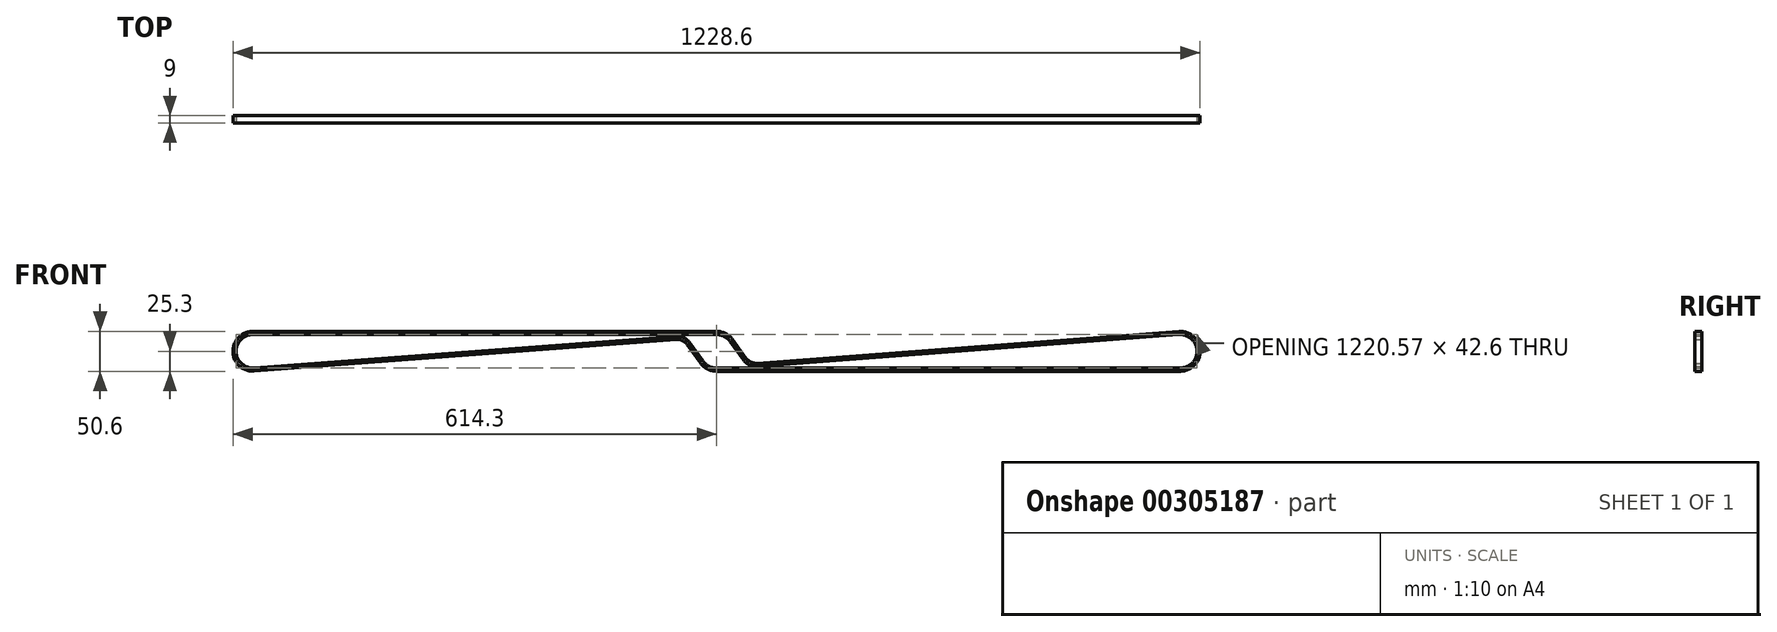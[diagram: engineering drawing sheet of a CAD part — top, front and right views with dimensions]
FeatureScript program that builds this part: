
annotation { "Feature Type Name" : "Feature", "Feature Type Description" : "" }
export const myFeature = defineFeature(function(context is Context, id is Id, definition is map)
    precondition{}
    {
        {
            var Q0;
            Q0=qCreatedBy(makeId("Front.planeOp"),FACE);
            var sketch = newSketch(context, id + "F0", { "sketchPlane" : qUnion([Q0])});
            skLineSegment(sketch, "E0", {"start": v(-36.07, 10.09) * mm, "end": v(-36.07, 10.09) * mm});
            skLineSegment(sketch, "E1", {"start": v(0, -23.3) * mm, "end": v(589, -23.3) * mm});
            skLineSegment(sketch, "E2", {"start": v(587.25, 23.23) * mm, "end": v(51.3, -17.15) * mm});
            skLineSegment(sketch, "E3", {"start": v(36.07, -10.09) * mm, "end": v(18.87, 13.66) * mm});
            skLineSegment(sketch, "E4", {"start": v(0, 23.3) * mm, "end": v(-589, 23.3) * mm});
            skLineSegment(sketch, "E5", {"start": v(-587.25, -23.23) * mm, "end": v(-51.3, 17.15) * mm});
            skArc(sketch, "E6", {"start": v(0, 23.3) * mm, "mid": v(-20.75, 10.6) * mm, "end": v(-18.87, -13.66) * mm});
            skArc(sketch, "E7", {"start": v(18.87, 13.66) * mm, "mid": v(10.6, 20.75) * mm, "end": v(0, 23.3) * mm});
            skArc(sketch, "E8", {"start": v(-18.87, -13.66) * mm, "mid": v(-10.6, -20.75) * mm, "end": v(0, -23.3) * mm});
            skArc(sketch, "E9", {"start": v(0, -23.3) * mm, "mid": v(20.75, -10.6) * mm, "end": v(18.87, 13.66) * mm});
            skLineSegment(sketch, "E10", {"start": v(-36.07, 10.09) * mm, "end": v(-18.87, -13.66) * mm});
            skArc(sketch, "E11", {"start": v(-51.3, 17.15) * mm, "mid": v(-57.24, -15.6) * mm, "end": v(-36.07, 10.09) * mm});
            skArc(sketch, "E12", {"start": v(-36.07, 10.09) * mm, "mid": v(-42.76, 15.6) * mm, "end": v(-51.3, 17.15) * mm});
            skArc(sketch, "E13", {"start": v(36.07, -10.09) * mm, "mid": v(42.76, -15.6) * mm, "end": v(51.3, -17.15) * mm});
            skArc(sketch, "E14", {"start": v(51.3, -17.15) * mm, "mid": v(57.24, 15.6) * mm, "end": v(36.07, -10.09) * mm});
            skArc(sketch, "E15", {"start": v(587.25, 23.23) * mm, "mid": v(565.72, -0.88) * mm, "end": v(589, -23.3) * mm});
            skArc(sketch, "E16", {"start": v(589, -23.3) * mm, "mid": v(612.28, 0.88) * mm, "end": v(587.25, 23.23) * mm});
            skArc(sketch, "E17", {"start": v(-589, 23.3) * mm, "mid": v(-612.28, -0.88) * mm, "end": v(-587.25, -23.23) * mm});
            skArc(sketch, "E18", {"start": v(-587.25, -23.23) * mm, "mid": v(-565.72, 0.88) * mm, "end": v(-589, 23.3) * mm});
            skPoint(sketch, "E19", {"position": v(-50, 5) * mm});
            skSolve(sketch);
        }
        {
            var Q0;
            Q0=sQuery(id+"F0.wireOp",EDGE,"E2");
            var Q1;
            Q1=sQuery(id+"F0.wireOp",VERTEX,"E2.start");
            cPlane(context, id + "F1", {"entities" : qUnion([Q0, Q1]), "cplaneType" : CPlaneType.CURVE_POINT, "offset" : 25 * mm, "width" : 150 * mm, "height" : 150 * mm});
        }
        {
            var Q0;
            Q0=qCreatedBy(id+"F1.planeOp",FACE);
            var sketch = newSketch(context, id + "F2", { "sketchPlane" : qUnion([Q0])});
            skLineSegment(sketch, "E20", {"start": v(4.5, -18.96) * mm, "end": v(-4.5, -18.96) * mm});
            skLineSegment(sketch, "E21", {"start": v(4.5, -22.96) * mm, "end": v(-4.5, -22.96) * mm});
            skLineSegment(sketch, "E22.0", {"start": v(4.5, -19.36) * mm, "end": v(4.5, -22.96) * mm});
            skLineSegment(sketch, "E23.0", {"start": v(4.5, -19.36) * mm, "end": v(4.5, -18.96) * mm});
            skLineSegment(sketch, "E24.0", {"start": v(-4.5, -18.96) * mm, "end": v(-4.5, -20.07) * mm});
            skLineSegment(sketch, "E25.0", {"start": v(-4.5, -22.96) * mm, "end": v(-4.5, -20.07) * mm});
            skPoint(sketch, "E26.orphan", {"position": v(4, -18.96) * mm});
            skPoint(sketch, "E27.orphan", {"position": v(4, -22.96) * mm});
            skSolve(sketch);
        }
        {
            var Q0;
            Q0=makeQuery(id+"F2.imprint","IMPRINT",FACE,{"disambiguationData":[TD([[makeQuery(id+"F2.imprint","IMPRINT",EDGE,{"derivedFrom":sQuery(id+"F2.wireOp",EDGE,"E20")}),1.0]])]});
            var Q1;
            Q1=sQuery(id+"F0.wireOp",EDGE,"E2");
            var Q2;
            Q2=sQuery(id+"F0.wireOp",EDGE,"E13");
            var Q3;
            Q3=sQuery(id+"F0.wireOp",EDGE,"E3");
            var Q4;
            Q4=sQuery(id+"F0.wireOp",EDGE,"E7");
            var Q5;
            Q5=sQuery(id+"F0.wireOp",EDGE,"E4");
            var Q6;
            Q6=sQuery(id+"F0.wireOp",EDGE,"E17");
            var Q7;
            Q7=sQuery(id+"F0.wireOp",EDGE,"E5");
            var Q8;
            Q8=sQuery(id+"F0.wireOp",EDGE,"E12");
            var Q9;
            Q9=sQuery(id+"F0.wireOp",EDGE,"E10");
            var Q10;
            Q10=sQuery(id+"F0.wireOp",EDGE,"E8");
            var Q11;
            Q11=sQuery(id+"F0.wireOp",EDGE,"E1");
            var Q12;
            Q12=sQuery(id+"F0.wireOp",EDGE,"E16");
            sweep(context, id + "F3", {"profiles" : qUnion([Q0]), "path" : qUnion([Q1, Q2, Q3, Q4, Q5, Q6, Q7, Q8, Q9, Q10, Q11, Q12])});
        }
    });
